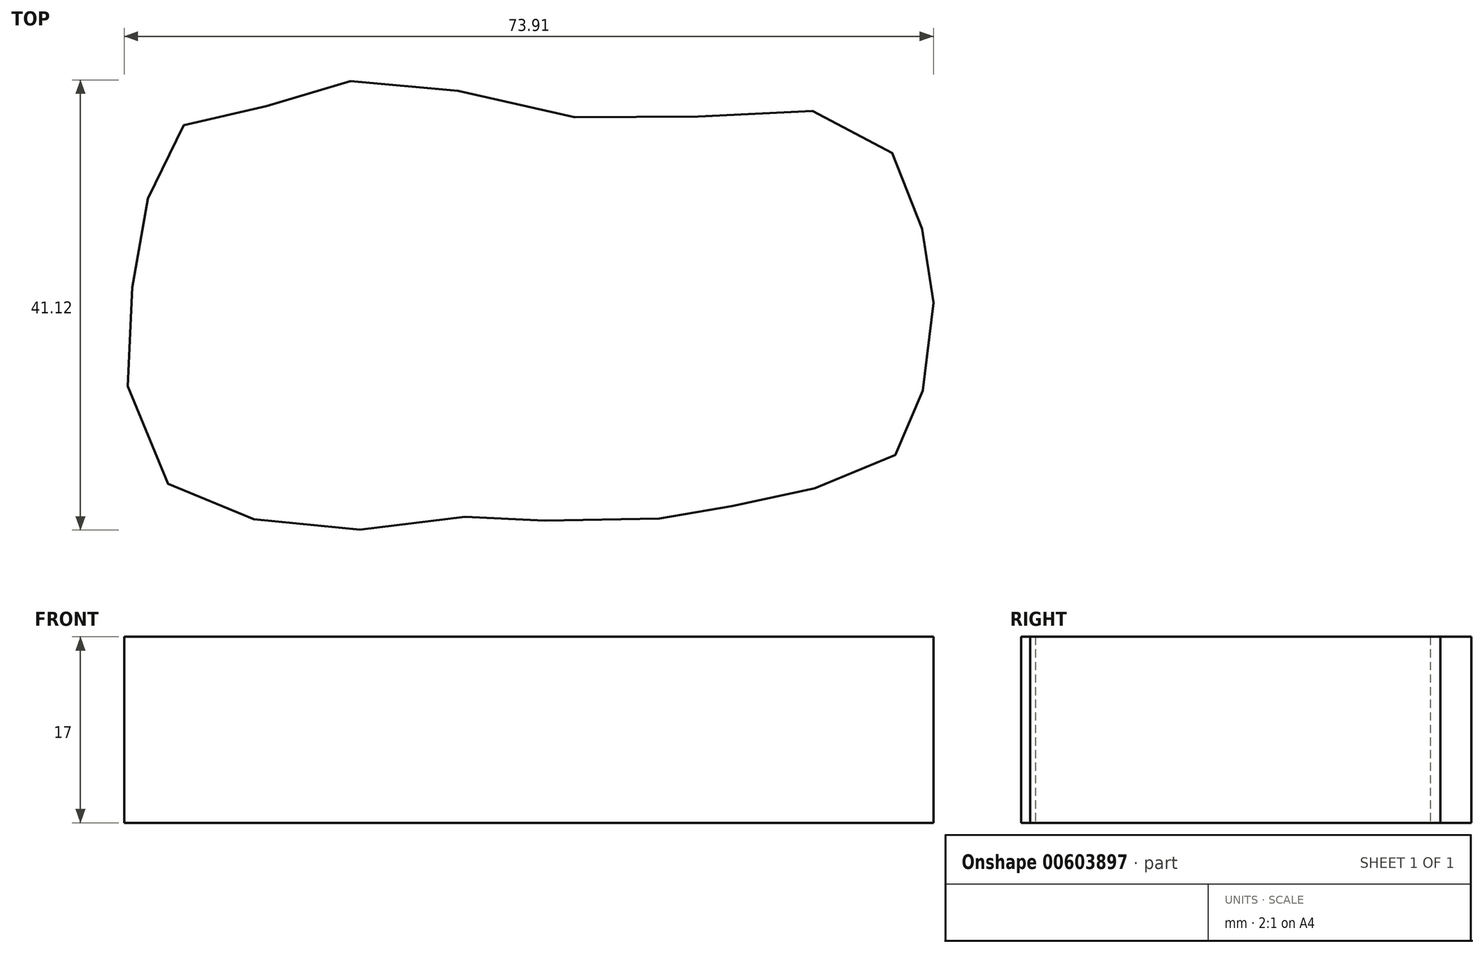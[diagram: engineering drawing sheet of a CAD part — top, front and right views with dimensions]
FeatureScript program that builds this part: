
annotation { "Feature Type Name" : "Feature", "Feature Type Description" : "" }
export const myFeature = defineFeature(function(context is Context, id is Id, definition is map)
    precondition{}
    {
        {
            var Q0;
            Q0=qCreatedBy(makeId("Top.planeOp"),FACE);
            var sketch = newSketch(context, id + "F0", { "sketchPlane" : qUnion([Q0])});
            skLineSegment(sketch, "E0", {"start": v(0, 53.43) * mm, "end": v(0, -68.16) * mm, "construction": true});
            skLineSegment(sketch, "E1", {"start": v(-72.86, 0) * mm, "end": v(75.94, 0) * mm, "construction": true});
            skFitSpline(sketch, "E2", {"points": [v(-39.04, 0) * mm, v(-38.6, 4) * mm, v(-37.1, 9.86) * mm, v(-35.69, 13.4) * mm, v(-32.77, 15.67) * mm, v(-28.54, 16.23) * mm, v(-23.26, 17.66) * mm, v(-19.35, 18.82) * mm, v(-13.37, 18.65) * mm, v(-4.59, 16.93) * mm, v(3.5, 15.3) * mm, v(12.9, 15.65) * mm, v(21.06, 16.13) * mm, v(26.93, 15.34) * mm, v(30.59, 12.05) * mm, v(32.62, 8.42) * mm, v(33.21, 4.47) * mm, v(33.92, 1) * mm, v(34.12, -2.08) * mm, v(33.45, -6.93) * mm, v(32.84, -11.14) * mm, v(31.7, -13.56) * mm, v(29.92, -16.08) * mm, v(25.22, -17.92) * mm, v(20.69, -18.9) * mm, v(16.45, -19.87) * mm, v(13.47, -20.22) * mm, v(10.41, -20.96) * mm, v(3.61, -21.28) * mm, v(-3.45, -21.19) * mm, v(-5.84, -20.84) * mm, v(-12.32, -21.42) * mm, v(-18.49, -22.13) * mm, v(-25.39, -21.68) * mm, v(-31.49, -20.17) * mm, v(-35.72, -17.98) * mm, v(-38.58, -12.72) * mm, v(-39.75, -4.67) * mm, v(-39.04, 0) * mm]});
            skSolve(sketch);
        }
        {
            var Q0;
            Q0 = qSketchRegion(id + "F0", true);
            extrude(context, id + "F1", {"entities" : qUnion([Q0]), "depth" : 17 * mm, "offsetDistance" : 25 * mm});
        }
    });
